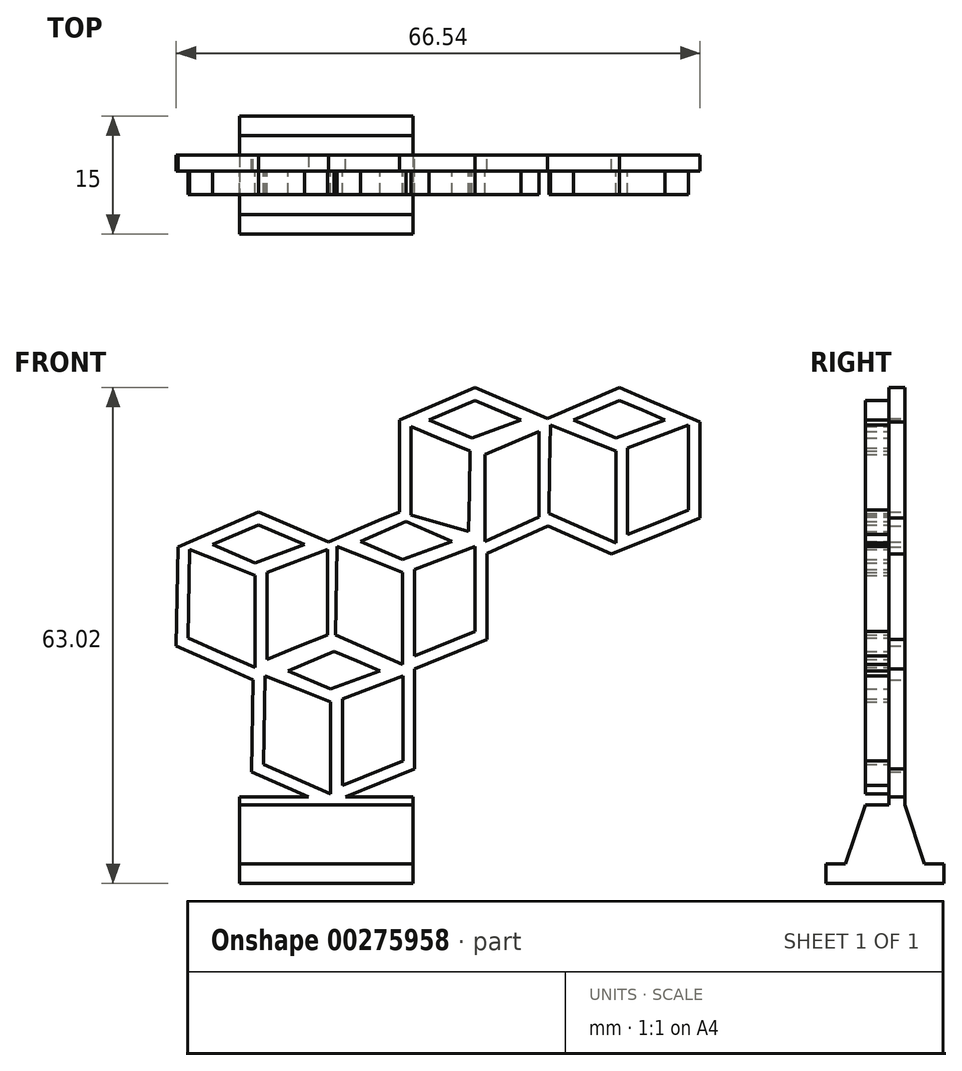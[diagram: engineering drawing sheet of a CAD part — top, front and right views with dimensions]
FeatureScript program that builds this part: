
annotation { "Feature Type Name" : "Feature", "Feature Type Description" : "" }
export const myFeature = defineFeature(function(context is Context, id is Id, definition is map)
    precondition{}
    {
        {
            var Q0;
            Q0=qCreatedBy(makeId("Front.planeOp"),FACE);
            var sketch = newSketch(context, id + "F0", { "sketchPlane" : qUnion([Q0])});
            skLineSegment(sketch, "E0", {"start": v(-13.23, -6.88) * mm, "end": v(-16.14, -8.13) * mm});
            skLineSegment(sketch, "E1", {"start": v(-16.14, -8.13) * mm, "end": v(-19.05, -9.38) * mm});
            skLineSegment(sketch, "E2", {"start": v(-19.05, -9.38) * mm, "end": v(-16.35, -10.53) * mm});
            skLineSegment(sketch, "E3", {"start": v(-16.35, -10.53) * mm, "end": v(-13.66, -11.68) * mm});
            skLineSegment(sketch, "E4", {"start": v(-13.66, -11.68) * mm, "end": v(-10.53, -10.53) * mm});
            skLineSegment(sketch, "E5", {"start": v(-10.53, -10.53) * mm, "end": v(-7.4, -9.38) * mm});
            skLineSegment(sketch, "E6", {"start": v(-7.4, -9.38) * mm, "end": v(-10.32, -8.13) * mm});
            skLineSegment(sketch, "E7", {"start": v(-10.32, -8.13) * mm, "end": v(-13.23, -6.88) * mm});
            skLineSegment(sketch, "E8", {"start": v(-21.98, -10) * mm, "end": v(-22.08, -15.62) * mm});
            skLineSegment(sketch, "E9", {"start": v(-22.08, -15.62) * mm, "end": v(-22.17, -21.25) * mm});
            skLineSegment(sketch, "E10", {"start": v(-22.17, -21.25) * mm, "end": v(-17.92, -23.12) * mm});
            skLineSegment(sketch, "E11", {"start": v(-17.92, -23.12) * mm, "end": v(-13.66, -25) * mm});
            skLineSegment(sketch, "E12", {"start": v(-13.66, -25) * mm, "end": v(-13.66, -19.16) * mm});
            skLineSegment(sketch, "E13", {"start": v(-13.66, -19.16) * mm, "end": v(-13.66, -13.32) * mm});
            skLineSegment(sketch, "E14", {"start": v(-13.66, -13.32) * mm, "end": v(-17.82, -11.66) * mm});
            skLineSegment(sketch, "E15", {"start": v(-17.82, -11.66) * mm, "end": v(-21.98, -10) * mm});
            skLineSegment(sketch, "E16", {"start": v(-4.48, -10) * mm, "end": v(-8.33, -11.47) * mm});
            skLineSegment(sketch, "E17", {"start": v(-8.33, -11.47) * mm, "end": v(-12.18, -12.93) * mm});
            skLineSegment(sketch, "E18", {"start": v(-12.18, -12.93) * mm, "end": v(-12.18, -18.44) * mm});
            skLineSegment(sketch, "E19", {"start": v(-12.18, -18.44) * mm, "end": v(-12.18, -23.95) * mm});
            skLineSegment(sketch, "E20", {"start": v(-12.18, -23.95) * mm, "end": v(-8.33, -22.38) * mm});
            skLineSegment(sketch, "E21", {"start": v(-8.33, -22.38) * mm, "end": v(-4.48, -20.82) * mm});
            skLineSegment(sketch, "E22", {"start": v(-4.48, -20.82) * mm, "end": v(-4.48, -15.41) * mm});
            skLineSegment(sketch, "E23", {"start": v(-4.48, -15.41) * mm, "end": v(-4.48, -10) * mm});
            skLineSegment(sketch, "E24", {"start": v(4.7, 25) * mm, "end": v(1.77, 23.75) * mm});
            skLineSegment(sketch, "E25", {"start": v(1.77, 23.75) * mm, "end": v(-1.16, 22.5) * mm});
            skLineSegment(sketch, "E26", {"start": v(-1.16, 22.5) * mm, "end": v(1.56, 21.35) * mm});
            skLineSegment(sketch, "E27", {"start": v(1.56, 21.35) * mm, "end": v(4.27, 20.2) * mm});
            skLineSegment(sketch, "E28", {"start": v(4.27, 20.2) * mm, "end": v(7.4, 21.35) * mm});
            skLineSegment(sketch, "E29", {"start": v(7.4, 21.35) * mm, "end": v(10.52, 22.5) * mm});
            skLineSegment(sketch, "E30", {"start": v(10.52, 22.5) * mm, "end": v(7.61, 23.75) * mm});
            skLineSegment(sketch, "E31", {"start": v(7.61, 23.75) * mm, "end": v(4.7, 25) * mm});
            skLineSegment(sketch, "E32", {"start": v(-3.42, 21.68) * mm, "end": v(-3.42, 16.05) * mm});
            skLineSegment(sketch, "E33", {"start": v(-3.42, 16.05) * mm, "end": v(-3.42, 10.43) * mm});
            skLineSegment(sketch, "E34", {"start": v(-3.42, 10.43) * mm, "end": v(0.2, 9.38) * mm});
            skLineSegment(sketch, "E35", {"start": v(0.2, 9.38) * mm, "end": v(3.84, 8.32) * mm});
            skLineSegment(sketch, "E36", {"start": v(3.84, 8.32) * mm, "end": v(3.96, 13.44) * mm});
            skLineSegment(sketch, "E37", {"start": v(3.96, 13.44) * mm, "end": v(4.08, 18.56) * mm});
            skLineSegment(sketch, "E38", {"start": v(4.08, 18.56) * mm, "end": v(0.33, 20.12) * mm});
            skLineSegment(sketch, "E39", {"start": v(0.33, 20.12) * mm, "end": v(-3.42, 21.68) * mm});
            skLineSegment(sketch, "E40", {"start": v(12.83, 21.05) * mm, "end": v(9.39, 19.6) * mm});
            skLineSegment(sketch, "E41", {"start": v(9.39, 19.6) * mm, "end": v(5.95, 18.13) * mm});
            skLineSegment(sketch, "E42", {"start": v(5.95, 18.13) * mm, "end": v(5.95, 12.6) * mm});
            skLineSegment(sketch, "E43", {"start": v(5.95, 12.6) * mm, "end": v(5.95, 7.07) * mm});
            skLineSegment(sketch, "E44", {"start": v(5.95, 7.07) * mm, "end": v(9.39, 8.63) * mm});
            skLineSegment(sketch, "E45", {"start": v(9.39, 8.63) * mm, "end": v(12.83, 10.2) * mm});
            skLineSegment(sketch, "E46", {"start": v(12.83, 10.2) * mm, "end": v(12.83, 15.63) * mm});
            skLineSegment(sketch, "E47", {"start": v(12.83, 15.63) * mm, "end": v(12.83, 21.05) * mm});
            skLineSegment(sketch, "E48", {"start": v(-22.82, 9.17) * mm, "end": v(-25.73, 7.92) * mm});
            skLineSegment(sketch, "E49", {"start": v(-25.73, 7.92) * mm, "end": v(-28.64, 6.67) * mm});
            skLineSegment(sketch, "E50", {"start": v(-28.64, 6.67) * mm, "end": v(-25.94, 5.51) * mm});
            skLineSegment(sketch, "E51", {"start": v(-25.94, 5.51) * mm, "end": v(-23.25, 4.36) * mm});
            skLineSegment(sketch, "E52", {"start": v(-23.25, 4.36) * mm, "end": v(-20.12, 5.51) * mm});
            skLineSegment(sketch, "E53", {"start": v(-20.12, 5.51) * mm, "end": v(-17, 6.67) * mm});
            skLineSegment(sketch, "E54", {"start": v(-17, 6.67) * mm, "end": v(-19.9, 7.92) * mm});
            skLineSegment(sketch, "E55", {"start": v(-19.9, 7.92) * mm, "end": v(-22.82, 9.17) * mm});
            skLineSegment(sketch, "E56", {"start": v(-31.57, 6.04) * mm, "end": v(-31.67, 0.42) * mm});
            skLineSegment(sketch, "E57", {"start": v(-31.67, 0.42) * mm, "end": v(-31.76, -5.2) * mm});
            skLineSegment(sketch, "E58", {"start": v(-31.76, -5.2) * mm, "end": v(-27.5, -7.08) * mm});
            skLineSegment(sketch, "E59", {"start": v(-27.5, -7.08) * mm, "end": v(-23.25, -8.96) * mm});
            skLineSegment(sketch, "E60", {"start": v(-23.25, -8.96) * mm, "end": v(-23.25, -3.12) * mm});
            skLineSegment(sketch, "E61", {"start": v(-23.25, -3.12) * mm, "end": v(-23.25, 2.72) * mm});
            skLineSegment(sketch, "E62", {"start": v(-23.25, 2.72) * mm, "end": v(-27.4, 4.38) * mm});
            skLineSegment(sketch, "E63", {"start": v(-27.4, 4.38) * mm, "end": v(-31.57, 6.04) * mm});
            skLineSegment(sketch, "E64", {"start": v(-14.07, 6.04) * mm, "end": v(-17.92, 4.58) * mm});
            skLineSegment(sketch, "E65", {"start": v(-17.92, 4.58) * mm, "end": v(-21.76, 3.11) * mm});
            skLineSegment(sketch, "E66", {"start": v(-21.76, 3.11) * mm, "end": v(-21.76, -2.4) * mm});
            skLineSegment(sketch, "E67", {"start": v(-21.76, -2.4) * mm, "end": v(-21.76, -7.9) * mm});
            skLineSegment(sketch, "E68", {"start": v(-21.76, -7.9) * mm, "end": v(-17.92, -6.34) * mm});
            skLineSegment(sketch, "E69", {"start": v(-17.92, -6.34) * mm, "end": v(-14.07, -4.78) * mm});
            skLineSegment(sketch, "E70", {"start": v(-14.07, -4.78) * mm, "end": v(-14.07, 0.63) * mm});
            skLineSegment(sketch, "E71", {"start": v(-14.07, 0.63) * mm, "end": v(-14.07, 6.04) * mm});
            skLineSegment(sketch, "E72", {"start": v(-4.07, 9.58) * mm, "end": v(-6.98, 8.33) * mm});
            skLineSegment(sketch, "E73", {"start": v(-6.98, 8.33) * mm, "end": v(-9.89, 7.08) * mm});
            skLineSegment(sketch, "E74", {"start": v(-9.89, 7.08) * mm, "end": v(-7.2, 5.93) * mm});
            skLineSegment(sketch, "E75", {"start": v(-7.2, 5.93) * mm, "end": v(-4.5, 4.78) * mm});
            skLineSegment(sketch, "E76", {"start": v(-4.5, 4.78) * mm, "end": v(-1.37, 5.93) * mm});
            skLineSegment(sketch, "E77", {"start": v(-1.37, 5.93) * mm, "end": v(1.75, 7.08) * mm});
            skLineSegment(sketch, "E78", {"start": v(1.75, 7.08) * mm, "end": v(-1.16, 8.33) * mm});
            skLineSegment(sketch, "E79", {"start": v(-1.16, 8.33) * mm, "end": v(-4.07, 9.58) * mm});
            skLineSegment(sketch, "E80", {"start": v(-12.82, 6.46) * mm, "end": v(-12.92, 0.83) * mm});
            skLineSegment(sketch, "E81", {"start": v(-12.92, 0.83) * mm, "end": v(-13.01, -4.8) * mm});
            skLineSegment(sketch, "E82", {"start": v(-13.01, -4.8) * mm, "end": v(-8.76, -6.67) * mm});
            skLineSegment(sketch, "E83", {"start": v(-8.76, -6.67) * mm, "end": v(-4.5, -8.54) * mm});
            skLineSegment(sketch, "E84", {"start": v(-4.5, -8.54) * mm, "end": v(-4.5, -2.7) * mm});
            skLineSegment(sketch, "E85", {"start": v(-4.5, -2.7) * mm, "end": v(-4.5, 3.14) * mm});
            skLineSegment(sketch, "E86", {"start": v(-4.5, 3.14) * mm, "end": v(-8.66, 4.8) * mm});
            skLineSegment(sketch, "E87", {"start": v(-8.66, 4.8) * mm, "end": v(-12.82, 6.46) * mm});
            skLineSegment(sketch, "E88", {"start": v(4.68, 6.46) * mm, "end": v(0.83, 5) * mm});
            skLineSegment(sketch, "E89", {"start": v(0.83, 5) * mm, "end": v(-3.01, 3.53) * mm});
            skLineSegment(sketch, "E90", {"start": v(-3.01, 3.53) * mm, "end": v(-3.01, -1.98) * mm});
            skLineSegment(sketch, "E91", {"start": v(-3.01, -1.98) * mm, "end": v(-3.01, -7.49) * mm});
            skLineSegment(sketch, "E92", {"start": v(-3.01, -7.49) * mm, "end": v(0.83, -5.93) * mm});
            skLineSegment(sketch, "E93", {"start": v(0.83, -5.93) * mm, "end": v(4.68, -4.36) * mm});
            skLineSegment(sketch, "E94", {"start": v(4.68, -4.36) * mm, "end": v(4.68, 1.05) * mm});
            skLineSegment(sketch, "E95", {"start": v(4.68, 1.05) * mm, "end": v(4.68, 6.46) * mm});
            skLineSegment(sketch, "E96", {"start": v(23.01, 25) * mm, "end": v(20.1, 23.75) * mm});
            skLineSegment(sketch, "E97", {"start": v(20.1, 23.75) * mm, "end": v(17.2, 22.5) * mm});
            skLineSegment(sketch, "E98", {"start": v(17.2, 22.5) * mm, "end": v(19.89, 21.35) * mm});
            skLineSegment(sketch, "E99", {"start": v(19.89, 21.35) * mm, "end": v(22.59, 20.2) * mm});
            skLineSegment(sketch, "E100", {"start": v(22.59, 20.2) * mm, "end": v(25.71, 21.35) * mm});
            skLineSegment(sketch, "E101", {"start": v(25.71, 21.35) * mm, "end": v(28.84, 22.5) * mm});
            skLineSegment(sketch, "E102", {"start": v(28.84, 22.5) * mm, "end": v(25.92, 23.75) * mm});
            skLineSegment(sketch, "E103", {"start": v(25.92, 23.75) * mm, "end": v(23.01, 25) * mm});
            skLineSegment(sketch, "E104", {"start": v(14.26, 21.87) * mm, "end": v(14.17, 16.25) * mm});
            skLineSegment(sketch, "E105", {"start": v(14.17, 16.25) * mm, "end": v(14.07, 10.62) * mm});
            skLineSegment(sketch, "E106", {"start": v(14.07, 10.62) * mm, "end": v(18.33, 8.75) * mm});
            skLineSegment(sketch, "E107", {"start": v(18.33, 8.75) * mm, "end": v(22.59, 6.88) * mm});
            skLineSegment(sketch, "E108", {"start": v(22.59, 6.88) * mm, "end": v(22.59, 12.72) * mm});
            skLineSegment(sketch, "E109", {"start": v(22.59, 12.72) * mm, "end": v(22.59, 18.56) * mm});
            skLineSegment(sketch, "E110", {"start": v(22.59, 18.56) * mm, "end": v(18.43, 20.21) * mm});
            skLineSegment(sketch, "E111", {"start": v(18.43, 20.21) * mm, "end": v(14.26, 21.87) * mm});
            skLineSegment(sketch, "E112", {"start": v(31.76, 21.87) * mm, "end": v(27.92, 20.4) * mm});
            skLineSegment(sketch, "E113", {"start": v(27.92, 20.4) * mm, "end": v(24.07, 18.95) * mm});
            skLineSegment(sketch, "E114", {"start": v(24.07, 18.95) * mm, "end": v(24.07, 13.44) * mm});
            skLineSegment(sketch, "E115", {"start": v(24.07, 13.44) * mm, "end": v(24.07, 7.93) * mm});
            skLineSegment(sketch, "E116", {"start": v(24.07, 7.93) * mm, "end": v(27.92, 9.5) * mm});
            skLineSegment(sketch, "E117", {"start": v(27.92, 9.5) * mm, "end": v(31.76, 11.05) * mm});
            skLineSegment(sketch, "E118", {"start": v(31.76, 11.05) * mm, "end": v(31.76, 16.46) * mm});
            skLineSegment(sketch, "E119", {"start": v(31.76, 16.46) * mm, "end": v(31.76, 21.87) * mm});
            skLineSegment(sketch, "E120.0", {"start": v(-26.32, 9.3) * mm, "end": v(-33.06, 6.4) * mm});
            skLineSegment(sketch, "E120.1", {"start": v(-22.82, 10.8) * mm, "end": v(-26.32, 9.3) * mm});
            skLineSegment(sketch, "E121.0", {"start": v(-33.17, 0.44) * mm, "end": v(-33.28, -6.18) * mm});
            skLineSegment(sketch, "E121.1", {"start": v(-33.06, 6.4) * mm, "end": v(-33.17, 0.44) * mm});
            skLineSegment(sketch, "E122.0", {"start": v(-19.32, 9.3) * mm, "end": v(-22.82, 10.8) * mm});
            skLineSegment(sketch, "E122.1", {"start": v(-13.93, 6.98) * mm, "end": v(-19.32, 9.3) * mm});
            skLineSegment(sketch, "E123.0", {"start": v(-7.57, 9.71) * mm, "end": v(-13.93, 6.98) * mm});
            skLineSegment(sketch, "E123.1", {"start": v(-4.66, 10.96) * mm, "end": v(-7.57, 9.71) * mm});
            skLineSegment(sketch, "E124.0", {"start": v(-4.92, 16.05) * mm, "end": v(-4.92, 10.43) * mm});
            skLineSegment(sketch, "E124.1", {"start": v(-4.92, 22.52) * mm, "end": v(-4.92, 16.05) * mm});
            skLineSegment(sketch, "E125.0", {"start": v(1.18, 25.13) * mm, "end": v(-4.92, 22.52) * mm});
            skLineSegment(sketch, "E125.1", {"start": v(4.7, 26.63) * mm, "end": v(1.18, 25.13) * mm});
            skLineSegment(sketch, "E126.0", {"start": v(8.2, 25.13) * mm, "end": v(4.7, 26.63) * mm});
            skLineSegment(sketch, "E126.1", {"start": v(13.86, 22.7) * mm, "end": v(8.2, 25.13) * mm});
            skLineSegment(sketch, "E127.0", {"start": v(19.51, 25.13) * mm, "end": v(13.86, 22.7) * mm});
            skLineSegment(sketch, "E127.1", {"start": v(23.01, 26.63) * mm, "end": v(19.51, 25.13) * mm});
            skLineSegment(sketch, "E128.0", {"start": v(26.52, 25.13) * mm, "end": v(23.01, 26.63) * mm});
            skLineSegment(sketch, "E128.1", {"start": v(33.26, 22.23) * mm, "end": v(26.52, 25.13) * mm});
            skLineSegment(sketch, "E129.0", {"start": v(33.26, 16.46) * mm, "end": v(33.26, 22.23) * mm});
            skLineSegment(sketch, "E129.1", {"start": v(33.26, 10.04) * mm, "end": v(33.26, 16.46) * mm});
            skLineSegment(sketch, "E130.0", {"start": v(28.48, 8.1) * mm, "end": v(33.26, 10.04) * mm});
            skLineSegment(sketch, "E130.1", {"start": v(22.03, 5.48) * mm, "end": v(28.48, 8.1) * mm});
            skLineSegment(sketch, "E131.0", {"start": v(17.72, 7.38) * mm, "end": v(22.03, 5.48) * mm});
            skLineSegment(sketch, "E131.1", {"start": v(13.93, 9.05) * mm, "end": v(17.72, 7.38) * mm});
            skLineSegment(sketch, "E132.0", {"start": v(10, 7.27) * mm, "end": v(13.93, 9.05) * mm});
            skLineSegment(sketch, "E132.1", {"start": v(6.18, 5.53) * mm, "end": v(10, 7.27) * mm});
            skLineSegment(sketch, "E133.0", {"start": v(6.18, 1.05) * mm, "end": v(6.18, 5.53) * mm});
            skLineSegment(sketch, "E133.1", {"start": v(6.18, -5.37) * mm, "end": v(6.18, 1.05) * mm});
            skLineSegment(sketch, "E134.0", {"start": v(1.4, -7.32) * mm, "end": v(6.18, -5.37) * mm});
            skLineSegment(sketch, "E134.1", {"start": v(-2.98, -9.1) * mm, "end": v(1.4, -7.32) * mm});
            skLineSegment(sketch, "E135.0", {"start": v(-2.98, -15.41) * mm, "end": v(-2.98, -9.1) * mm});
            skLineSegment(sketch, "E135.1", {"start": v(-2.98, -21.83) * mm, "end": v(-2.98, -15.41) * mm});
            skLineSegment(sketch, "E136.0", {"start": v(-7.76, -23.77) * mm, "end": v(-2.98, -21.83) * mm});
            skLineSegment(sketch, "E136.1", {"start": v(-14.22, -26.4) * mm, "end": v(-7.76, -23.77) * mm});
            skLineSegment(sketch, "E137.0", {"start": v(-18.52, -24.5) * mm, "end": v(-14.22, -26.4) * mm});
            skLineSegment(sketch, "E137.1", {"start": v(-23.7, -22.22) * mm, "end": v(-18.52, -24.5) * mm});
            skLineSegment(sketch, "E138.0", {"start": v(-23.58, -15.6) * mm, "end": v(-23.7, -22.22) * mm});
            skLineSegment(sketch, "E138.1", {"start": v(-23.49, -10.5) * mm, "end": v(-23.58, -15.6) * mm});
            skLineSegment(sketch, "E139.0", {"start": v(-28.11, -8.46) * mm, "end": v(-23.49, -10.5) * mm});
            skLineSegment(sketch, "E139.1", {"start": v(-33.28, -6.18) * mm, "end": v(-28.11, -8.46) * mm});
            skLineSegment(sketch, "E140", {"start": v(-25.22, -26.4) * mm, "end": v(-3.22, -26.4) * mm});
            skSolve(sketch);
        }
        {
            var Q0;
            Q0=makeQuery(id+"F0.imprint","IMPRINT",FACE,{"disambiguationData":[TD([[makeQuery(id+"F0.imprint","IMPRINT",EDGE,{"derivedFrom":sQuery(id+"F0.wireOp",EDGE,"E0")}),-1.0]])]});
            var Q1;
            Q1=makeQuery(id+"F0.imprint","IMPRINT",FACE,{"disambiguationData":[TD([[makeQuery(id+"F0.imprint","IMPRINT",EDGE,{"derivedFrom":sQuery(id+"F0.wireOp",EDGE,"E104")}),1.0]])]});
            var Q2;
            Q2=makeQuery(id+"F0.imprint","IMPRINT",FACE,{"disambiguationData":[TD([[makeQuery(id+"F0.imprint","IMPRINT",EDGE,{"derivedFrom":sQuery(id+"F0.wireOp",EDGE,"E112")}),1.0]])]});
            var Q3;
            Q3=makeQuery(id+"F0.imprint","IMPRINT",FACE,{"disambiguationData":[TD([[makeQuery(id+"F0.imprint","IMPRINT",EDGE,{"derivedFrom":sQuery(id+"F0.wireOp",EDGE,"E0")}),1.0]])]});
            var Q4;
            Q4=makeQuery(id+"F0.imprint","IMPRINT",FACE,{"disambiguationData":[TD([[makeQuery(id+"F0.imprint","IMPRINT",EDGE,{"derivedFrom":sQuery(id+"F0.wireOp",EDGE,"E8")}),1.0]])]});
            var Q5;
            Q5=makeQuery(id+"F0.imprint","IMPRINT",FACE,{"disambiguationData":[TD([[makeQuery(id+"F0.imprint","IMPRINT",EDGE,{"derivedFrom":sQuery(id+"F0.wireOp",EDGE,"E16")}),1.0]])]});
            var Q6;
            Q6=makeQuery(id+"F0.imprint","IMPRINT",FACE,{"disambiguationData":[TD([[makeQuery(id+"F0.imprint","IMPRINT",EDGE,{"derivedFrom":sQuery(id+"F0.wireOp",EDGE,"E24")}),1.0]])]});
            var Q7;
            Q7=makeQuery(id+"F0.imprint","IMPRINT",FACE,{"disambiguationData":[TD([[makeQuery(id+"F0.imprint","IMPRINT",EDGE,{"derivedFrom":sQuery(id+"F0.wireOp",EDGE,"E32")}),1.0]])]});
            var Q8;
            Q8=makeQuery(id+"F0.imprint","IMPRINT",FACE,{"disambiguationData":[TD([[makeQuery(id+"F0.imprint","IMPRINT",EDGE,{"derivedFrom":sQuery(id+"F0.wireOp",EDGE,"E40")}),1.0]])]});
            var Q9;
            Q9=makeQuery(id+"F0.imprint","IMPRINT",FACE,{"disambiguationData":[TD([[makeQuery(id+"F0.imprint","IMPRINT",EDGE,{"derivedFrom":sQuery(id+"F0.wireOp",EDGE,"E48")}),1.0]])]});
            var Q10;
            Q10=makeQuery(id+"F0.imprint","IMPRINT",FACE,{"disambiguationData":[TD([[makeQuery(id+"F0.imprint","IMPRINT",EDGE,{"derivedFrom":sQuery(id+"F0.wireOp",EDGE,"E56")}),1.0]])]});
            var Q11;
            Q11=makeQuery(id+"F0.imprint","IMPRINT",FACE,{"disambiguationData":[TD([[makeQuery(id+"F0.imprint","IMPRINT",EDGE,{"derivedFrom":sQuery(id+"F0.wireOp",EDGE,"E64")}),1.0]])]});
            var Q12;
            Q12=makeQuery(id+"F0.imprint","IMPRINT",FACE,{"disambiguationData":[TD([[makeQuery(id+"F0.imprint","IMPRINT",EDGE,{"derivedFrom":sQuery(id+"F0.wireOp",EDGE,"E72")}),1.0]])]});
            var Q13;
            Q13=makeQuery(id+"F0.imprint","IMPRINT",FACE,{"disambiguationData":[TD([[makeQuery(id+"F0.imprint","IMPRINT",EDGE,{"derivedFrom":sQuery(id+"F0.wireOp",EDGE,"E80")}),1.0]])]});
            var Q14;
            Q14=makeQuery(id+"F0.imprint","IMPRINT",FACE,{"disambiguationData":[TD([[makeQuery(id+"F0.imprint","IMPRINT",EDGE,{"derivedFrom":sQuery(id+"F0.wireOp",EDGE,"E88")}),1.0]])]});
            var Q15;
            Q15=makeQuery(id+"F0.imprint","IMPRINT",FACE,{"disambiguationData":[TD([[makeQuery(id+"F0.imprint","IMPRINT",EDGE,{"derivedFrom":sQuery(id+"F0.wireOp",EDGE,"E96")}),1.0]])]});
            extrude(context, id + "F1", {"entities" : qUnion([Q0, Q1, Q2, Q3, Q4, Q5, Q6, Q7, Q8, Q9, Q10, Q11, Q12, Q13, Q14, Q15]), "depth" : 2 * mm});
        }
        {
            var Q0;
            Q0=makeQuery(id+"F0.imprint","IMPRINT",FACE,{"disambiguationData":[TD([[makeQuery(id+"F0.imprint","IMPRINT",EDGE,{"derivedFrom":sQuery(id+"F0.wireOp",EDGE,"E56")}),1.0]])]});
            var Q1;
            Q1=makeQuery(id+"F0.imprint","IMPRINT",FACE,{"disambiguationData":[TD([[makeQuery(id+"F0.imprint","IMPRINT",EDGE,{"derivedFrom":sQuery(id+"F0.wireOp",EDGE,"E48")}),1.0]])]});
            var Q2;
            Q2=makeQuery(id+"F0.imprint","IMPRINT",FACE,{"disambiguationData":[TD([[makeQuery(id+"F0.imprint","IMPRINT",EDGE,{"derivedFrom":sQuery(id+"F0.wireOp",EDGE,"E64")}),1.0]])]});
            var Q3;
            Q3=makeQuery(id+"F0.imprint","IMPRINT",FACE,{"disambiguationData":[TD([[makeQuery(id+"F0.imprint","IMPRINT",EDGE,{"derivedFrom":sQuery(id+"F0.wireOp",EDGE,"E0")}),1.0]])]});
            var Q4;
            Q4=makeQuery(id+"F0.imprint","IMPRINT",FACE,{"disambiguationData":[TD([[makeQuery(id+"F0.imprint","IMPRINT",EDGE,{"derivedFrom":sQuery(id+"F0.wireOp",EDGE,"E8")}),1.0]])]});
            var Q5;
            Q5=makeQuery(id+"F0.imprint","IMPRINT",FACE,{"disambiguationData":[TD([[makeQuery(id+"F0.imprint","IMPRINT",EDGE,{"derivedFrom":sQuery(id+"F0.wireOp",EDGE,"E16")}),1.0]])]});
            var Q6;
            Q6=makeQuery(id+"F0.imprint","IMPRINT",FACE,{"disambiguationData":[TD([[makeQuery(id+"F0.imprint","IMPRINT",EDGE,{"derivedFrom":sQuery(id+"F0.wireOp",EDGE,"E88")}),1.0]])]});
            var Q7;
            Q7=makeQuery(id+"F0.imprint","IMPRINT",FACE,{"disambiguationData":[TD([[makeQuery(id+"F0.imprint","IMPRINT",EDGE,{"derivedFrom":sQuery(id+"F0.wireOp",EDGE,"E80")}),1.0]])]});
            var Q8;
            Q8=makeQuery(id+"F0.imprint","IMPRINT",FACE,{"disambiguationData":[TD([[makeQuery(id+"F0.imprint","IMPRINT",EDGE,{"derivedFrom":sQuery(id+"F0.wireOp",EDGE,"E72")}),1.0]])]});
            var Q9;
            Q9=makeQuery(id+"F0.imprint","IMPRINT",FACE,{"disambiguationData":[TD([[makeQuery(id+"F0.imprint","IMPRINT",EDGE,{"derivedFrom":sQuery(id+"F0.wireOp",EDGE,"E32")}),1.0]])]});
            var Q10;
            Q10=makeQuery(id+"F0.imprint","IMPRINT",FACE,{"disambiguationData":[TD([[makeQuery(id+"F0.imprint","IMPRINT",EDGE,{"derivedFrom":sQuery(id+"F0.wireOp",EDGE,"E24")}),1.0]])]});
            var Q11;
            Q11=makeQuery(id+"F0.imprint","IMPRINT",FACE,{"disambiguationData":[TD([[makeQuery(id+"F0.imprint","IMPRINT",EDGE,{"derivedFrom":sQuery(id+"F0.wireOp",EDGE,"E40")}),1.0]])]});
            var Q12;
            Q12=makeQuery(id+"F0.imprint","IMPRINT",FACE,{"disambiguationData":[TD([[makeQuery(id+"F0.imprint","IMPRINT",EDGE,{"derivedFrom":sQuery(id+"F0.wireOp",EDGE,"E96")}),1.0]])]});
            var Q13;
            Q13=makeQuery(id+"F0.imprint","IMPRINT",FACE,{"disambiguationData":[TD([[makeQuery(id+"F0.imprint","IMPRINT",EDGE,{"derivedFrom":sQuery(id+"F0.wireOp",EDGE,"E104")}),1.0]])]});
            var Q14;
            Q14=makeQuery(id+"F0.imprint","IMPRINT",FACE,{"disambiguationData":[TD([[makeQuery(id+"F0.imprint","IMPRINT",EDGE,{"derivedFrom":sQuery(id+"F0.wireOp",EDGE,"E112")}),1.0]])]});
            extrude(context, id + "F2", {"entities" : qUnion([Q0, Q1, Q2, Q3, Q4, Q5, Q6, Q7, Q8, Q9, Q10, Q11, Q12, Q13, Q14]), "operationType" : NewBodyOperationType.ADD, "depth" : 5 * mm});
        }
        {
            var Q0;
            Q0=sQuery(id+"F0.wireOp",EDGE,"E140");
            var Q1;
            Q1=sQuery(id+"F0.wireOp",VERTEX,"E140.end");
            cPlane(context, id + "F3", {"entities" : qUnion([Q0, Q1]), "cplaneType" : CPlaneType.LINE_POINT, "offset" : 25 * mm, "width" : 150 * mm, "height" : 150 * mm});
        }
        {
            var Q0;
            Q0=qCreatedBy(id+"F3.planeOp",FACE);
            var sketch = newSketch(context, id + "F4", { "sketchPlane" : qUnion([Q0])});
            skLineSegment(sketch, "E141.bottom", {"start": v(0, -25.4) * mm, "end": v(-2, -25.4) * mm});
            skLineSegment(sketch, "E141.top", {"start": v(0, -26.4) * mm, "end": v(-2, -26.4) * mm});
            skLineSegment(sketch, "E141.left", {"start": v(0, -25.4) * mm, "end": v(0, -26.4) * mm});
            skLineSegment(sketch, "E141.right", {"start": v(-2, -25.4) * mm, "end": v(-2, -26.4) * mm});
            skLineSegment(sketch, "E142", {"start": v(0, -26.4) * mm, "end": v(2.5, -33.9) * mm});
            skLineSegment(sketch, "E143", {"start": v(2.5, -33.9) * mm, "end": v(5, -33.9) * mm});
            skLineSegment(sketch, "E144", {"start": v(5, -33.9) * mm, "end": v(5, -36.4) * mm});
            skLineSegment(sketch, "E145", {"start": v(5, -36.4) * mm, "end": v(-10, -36.4) * mm});
            skLineSegment(sketch, "E146", {"start": v(-10, -36.4) * mm, "end": v(-10, -33.9) * mm});
            skLineSegment(sketch, "E147", {"start": v(-10, -33.9) * mm, "end": v(-7.5, -33.9) * mm});
            skLineSegment(sketch, "E148", {"start": v(-7.5, -33.9) * mm, "end": v(-5, -26.4) * mm});
            skLineSegment(sketch, "E149", {"start": v(-5, -26.4) * mm, "end": v(-2, -26.4) * mm});
            skLineSegment(sketch, "E150", {"start": v(-2.5, -36.4) * mm, "end": v(-2.5, -26.4) * mm});
            skSolve(sketch);
        }
        {
            var Q0;
            {var subQ2=sQuery(id+"F4.wireOp",EDGE,"E141.top");Q0=makeQuery(id+"F4.imprint","IMPRINT",FACE,{"disambiguationData":[TD([[makeQuery(id+"F4.imprint","IMPRINT",EDGE,{"derivedFrom":subQ2}),1.0]])]});}
            var Q1;
            {var subQ1=sQuery(id+"F4.wireOp",EDGE,"E146");Q1=makeQuery(id+"F4.imprint","IMPRINT",FACE,{"disambiguationData":[TD([[makeQuery(id+"F4.imprint","IMPRINT",EDGE,{"derivedFrom":subQ1}),-1.0]])]});}
            var Q2;
            Q2=makeQuery(id+"F4.imprint","IMPRINT",FACE,{"disambiguationData":[TD([[makeQuery(id+"F4.imprint","IMPRINT",EDGE,{"derivedFrom":sQuery(id+"F4.wireOp",EDGE,"E141.bottom")}),1.0]])]});
            extrude(context, id + "F5", {"entities" : qUnion([Q0, Q1, Q2]), "operationType" : NewBodyOperationType.ADD, "oppositeDirection" : true, "depth" : 22 * mm});
        }
    });
